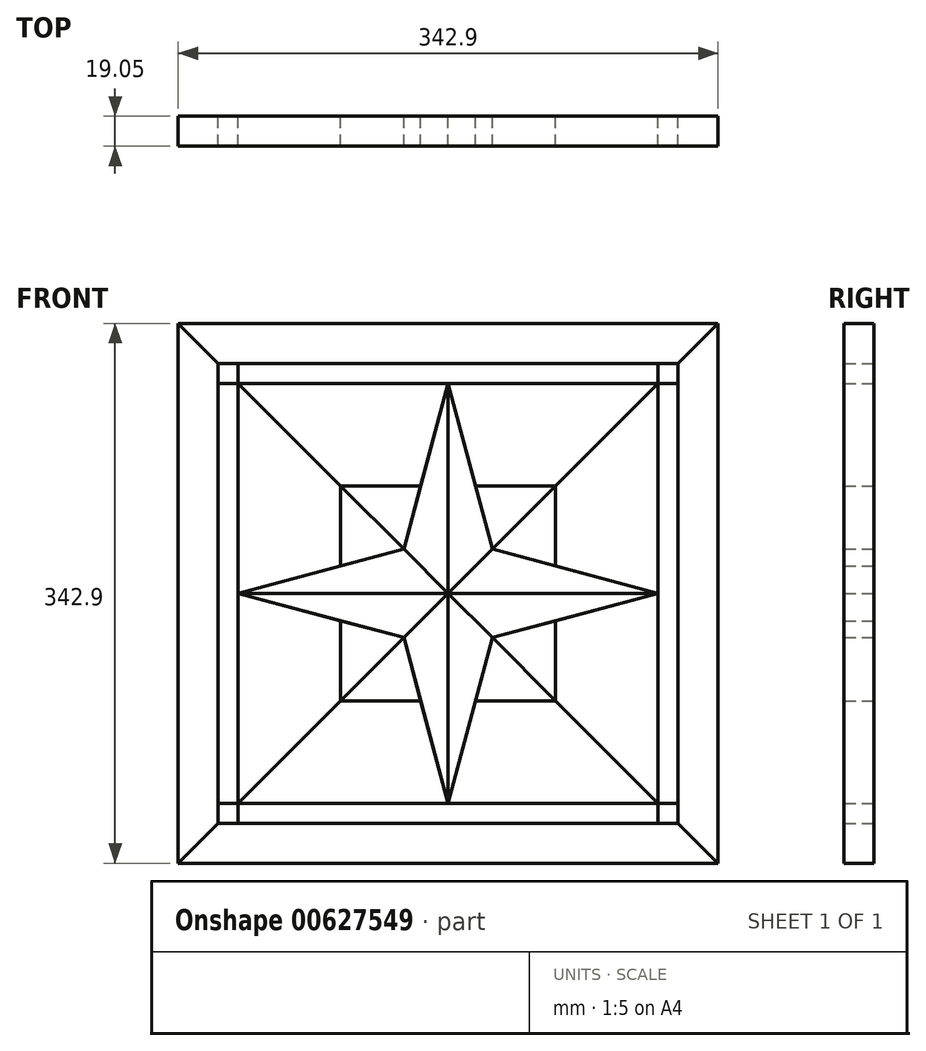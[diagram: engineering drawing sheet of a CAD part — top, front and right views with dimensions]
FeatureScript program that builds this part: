
annotation { "Feature Type Name" : "Feature", "Feature Type Description" : "" }
export const myFeature = defineFeature(function(context is Context, id is Id, definition is map)
    precondition{}
    {
        {
            var Q0;
            Q0=qCreatedBy(makeId("Front.planeOp"),FACE);
            var sketch = newSketch(context, id + "F0", { "sketchPlane" : qUnion([Q0])});
            skLineSegment(sketch, "E0", {"start": v(0, 133.35) * mm, "end": v(-28.18, 28.18) * mm});
            skLineSegment(sketch, "E1", {"start": v(-28.18, 28.18) * mm, "end": v(-133.35, 0) * mm});
            skLineSegment(sketch, "E2", {"start": v(-133.35, 0) * mm, "end": v(-28.18, -28.18) * mm});
            skLineSegment(sketch, "E3", {"start": v(-28.18, -28.18) * mm, "end": v(0, -133.35) * mm});
            skLineSegment(sketch, "E4", {"start": v(0, -133.35) * mm, "end": v(28.18, -28.18) * mm});
            skLineSegment(sketch, "E5", {"start": v(28.18, -28.18) * mm, "end": v(133.35, 0) * mm});
            skLineSegment(sketch, "E6", {"start": v(133.35, 0) * mm, "end": v(28.18, 28.18) * mm});
            skLineSegment(sketch, "E7", {"start": v(28.18, 28.18) * mm, "end": v(0, 133.35) * mm});
            skLineSegment(sketch, "E8", {"start": v(0, 133.35) * mm, "end": v(0, 0) * mm});
            skLineSegment(sketch, "E9", {"start": v(0, 0) * mm, "end": v(-28.18, 28.18) * mm});
            skLineSegment(sketch, "E10", {"start": v(0, 0) * mm, "end": v(28.18, 28.18) * mm});
            skLineSegment(sketch, "E11", {"start": v(0, 0) * mm, "end": v(-28.18, -28.18) * mm});
            skLineSegment(sketch, "E12", {"start": v(0, 0) * mm, "end": v(-133.35, 0) * mm});
            skLineSegment(sketch, "E13", {"start": v(0, 0) * mm, "end": v(28.18, -28.18) * mm});
            skLineSegment(sketch, "E14", {"start": v(0, 0) * mm, "end": v(133.35, 0) * mm});
            skLineSegment(sketch, "E15", {"start": v(17.44, 68.24) * mm, "end": v(68.24, 68.24) * mm});
            skLineSegment(sketch, "E16", {"start": v(68.24, 68.24) * mm, "end": v(68.24, 17.44) * mm});
            skLineSegment(sketch, "E17", {"start": v(28.18, 28.18) * mm, "end": v(68.24, 68.24) * mm});
            skLineSegment(sketch, "E18", {"start": v(-17.44, 68.24) * mm, "end": v(-68.24, 68.24) * mm});
            skLineSegment(sketch, "E19", {"start": v(-68.24, 68.24) * mm, "end": v(-68.24, 17.44) * mm});
            skLineSegment(sketch, "E20", {"start": v(-68.24, 68.24) * mm, "end": v(-28.18, 28.18) * mm});
            skLineSegment(sketch, "E21", {"start": v(0, 0) * mm, "end": v(0, -133.35) * mm});
            skLineSegment(sketch, "E22", {"start": v(-68.24, -17.44) * mm, "end": v(-68.24, -68.24) * mm});
            skLineSegment(sketch, "E23", {"start": v(-68.24, -68.24) * mm, "end": v(-17.44, -68.24) * mm});
            skLineSegment(sketch, "E24", {"start": v(-68.24, -68.24) * mm, "end": v(-28.18, -28.18) * mm});
            skLineSegment(sketch, "E25", {"start": v(17.44, -68.24) * mm, "end": v(68.24, -68.24) * mm});
            skLineSegment(sketch, "E26", {"start": v(68.24, -68.24) * mm, "end": v(68.24, -17.44) * mm});
            skLineSegment(sketch, "E27", {"start": v(68.24, -17.44) * mm, "end": v(28.18, -28.18) * mm});
            skLineSegment(sketch, "E28", {"start": v(68.24, -68.24) * mm, "end": v(28.18, -28.18) * mm});
            skLineSegment(sketch, "E29.bottom", {"start": v(171.45, -171.45) * mm, "end": v(-171.45, -171.45) * mm});
            skLineSegment(sketch, "E29.top", {"start": v(171.45, 171.45) * mm, "end": v(-171.45, 171.45) * mm});
            skLineSegment(sketch, "E29.left", {"start": v(171.45, -171.45) * mm, "end": v(171.45, 171.45) * mm});
            skLineSegment(sketch, "E29.right", {"start": v(-171.45, -171.45) * mm, "end": v(-171.45, 171.45) * mm});
            skPoint(sketch, "E29.middle", {"position": v(0, 0) * mm});
            skLineSegment(sketch, "E30", {"start": v(-171.45, 171.45) * mm, "end": v(-146.05, 146.05) * mm});
            skLineSegment(sketch, "E31", {"start": v(-146.05, 146.05) * mm, "end": v(-146.05, -146.05) * mm});
            skLineSegment(sketch, "E32", {"start": v(-146.05, -146.05) * mm, "end": v(-171.45, -171.45) * mm});
            skLineSegment(sketch, "E33", {"start": v(-146.05, 146.05) * mm, "end": v(146.05, 146.05) * mm});
            skLineSegment(sketch, "E34", {"start": v(146.05, 146.05) * mm, "end": v(171.45, 171.45) * mm});
            skLineSegment(sketch, "E35", {"start": v(146.05, 146.05) * mm, "end": v(146.05, -146.05) * mm});
            skLineSegment(sketch, "E36", {"start": v(146.05, -146.05) * mm, "end": v(-146.05, -146.05) * mm});
            skLineSegment(sketch, "E37", {"start": v(146.05, -146.05) * mm, "end": v(171.45, -171.45) * mm});
            skLineSegment(sketch, "E38", {"start": v(-133.35, 146.05) * mm, "end": v(-133.35, -146.05) * mm});
            skLineSegment(sketch, "E39", {"start": v(-146.05, 133.35) * mm, "end": v(146.05, 133.35) * mm});
            skLineSegment(sketch, "E40", {"start": v(133.35, 146.05) * mm, "end": v(133.35, -146.05) * mm});
            skLineSegment(sketch, "E41", {"start": v(-146.05, -133.35) * mm, "end": v(133.35, -133.35) * mm});
            skLineSegment(sketch, "E42", {"start": v(133.35, -133.35) * mm, "end": v(146.05, -133.35) * mm});
            skSolve(sketch);
        }
        {
            var Q0;
            Q0=makeQuery(id+"F0.imprint","IMPRINT",FACE,{"disambiguationData":[TD([[makeQuery(id+"F0.imprint","IMPRINT",EDGE,{"derivedFrom":sQuery(id+"F0.wireOp",EDGE,"E29.left")}),1.0]])]});
            var Q1;
            Q1=makeQuery(id+"F0.imprint","IMPRINT",FACE,{"disambiguationData":[TD([[makeQuery(id+"F0.imprint","IMPRINT",EDGE,{"derivedFrom":sQuery(id+"F0.wireOp",EDGE,"E29.right")}),-1.0]])]});
            extrude(context, id + "F1", {"entities" : qUnion([Q0, Q1]), "depth" : 19.05 * mm, "offsetDistance" : 25.4 * mm});
        }
        {
            var Q0;
            Q0=makeQuery(id+"F0.imprint","IMPRINT",FACE,{"disambiguationData":[TD([[makeQuery(id+"F0.imprint","IMPRINT",EDGE,{"derivedFrom":sQuery(id+"F0.wireOp",EDGE,"E29.top")}),1.0]])]});
            var Q1;
            Q1=makeQuery(id+"F0.imprint","IMPRINT",FACE,{"disambiguationData":[TD([[makeQuery(id+"F0.imprint","IMPRINT",EDGE,{"derivedFrom":sQuery(id+"F0.wireOp",EDGE,"E29.bottom")}),-1.0]])]});
            extrude(context, id + "F2", {"entities" : qUnion([Q0, Q1]), "depth" : 19.05 * mm, "offsetDistance" : 25.4 * mm});
        }
        {
            var Q0;
            {var subQ0=sQuery(id+"F0.wireOp",EDGE,"E8");Q0=makeQuery(id+"F0.imprint","IMPRINT",FACE,{"disambiguationData":[TD([[makeQuery(id+"F0.imprint","IMPRINT",EDGE,{"derivedFrom":subQ0}),-1.0]])]});}
            var Q1;
            {var subQ3=sQuery(id+"F0.wireOp",EDGE,"E10");Q1=makeQuery(id+"F0.imprint","IMPRINT",FACE,{"disambiguationData":[TD([[makeQuery(id+"F0.imprint","IMPRINT",EDGE,{"derivedFrom":subQ3}),-1.0]])]});}
            var Q2;
            {var subQ3=sQuery(id+"F0.wireOp",EDGE,"E13");Q2=makeQuery(id+"F0.imprint","IMPRINT",FACE,{"disambiguationData":[TD([[makeQuery(id+"F0.imprint","IMPRINT",EDGE,{"derivedFrom":subQ3}),-1.0]])]});}
            var Q3;
            {var subQ3=sQuery(id+"F0.wireOp",EDGE,"E11");Q3=makeQuery(id+"F0.imprint","IMPRINT",FACE,{"disambiguationData":[TD([[makeQuery(id+"F0.imprint","IMPRINT",EDGE,{"derivedFrom":subQ3}),-1.0]])]});}
            extrude(context, id + "F3", {"entities" : qUnion([Q0, Q1, Q2, Q3]), "depth" : 19.05 * mm, "offsetDistance" : 25.4 * mm});
        }
        {
            var Q0;
            {var subQ2=sQuery(id+"F0.wireOp",EDGE,"E15");Q0=makeQuery(id+"F0.imprint","IMPRINT",FACE,{"disambiguationData":[TD([[makeQuery(id+"F0.imprint","IMPRINT",EDGE,{"derivedFrom":subQ2}),-1.0]])]});}
            var Q1;
            Q1=makeQuery(id+"F0.imprint","IMPRINT",FACE,{"disambiguationData":[TD([[makeQuery(id+"F0.imprint","IMPRINT",EDGE,{"derivedFrom":sQuery(id+"F0.wireOp",EDGE,"E26")}),1.0]])]});
            var Q2;
            {var subQ2=sQuery(id+"F0.wireOp",EDGE,"E23");Q2=makeQuery(id+"F0.imprint","IMPRINT",FACE,{"disambiguationData":[TD([[makeQuery(id+"F0.imprint","IMPRINT",EDGE,{"derivedFrom":subQ2}),1.0]])]});}
            var Q3;
            {var subQ2=sQuery(id+"F0.wireOp",EDGE,"E19");Q3=makeQuery(id+"F0.imprint","IMPRINT",FACE,{"disambiguationData":[TD([[makeQuery(id+"F0.imprint","IMPRINT",EDGE,{"derivedFrom":subQ2}),1.0]])]});}
            extrude(context, id + "F4", {"entities" : qUnion([Q0, Q1, Q2, Q3]), "depth" : 19.05 * mm, "offsetDistance" : 25.4 * mm});
        }
        {
            var Q0;
            {var subQ2=sQuery(id+"F0.wireOp",EDGE,"E18");Q0=makeQuery(id+"F0.imprint","IMPRINT",FACE,{"disambiguationData":[TD([[makeQuery(id+"F0.imprint","IMPRINT",EDGE,{"derivedFrom":subQ2}),1.0]])]});}
            var Q1;
            {var subQ2=sQuery(id+"F0.wireOp",EDGE,"E16");Q1=makeQuery(id+"F0.imprint","IMPRINT",FACE,{"disambiguationData":[TD([[makeQuery(id+"F0.imprint","IMPRINT",EDGE,{"derivedFrom":subQ2}),-1.0]])]});}
            var Q2;
            {var subQ2=sQuery(id+"F0.wireOp",EDGE,"E25");Q2=makeQuery(id+"F0.imprint","IMPRINT",FACE,{"disambiguationData":[TD([[makeQuery(id+"F0.imprint","IMPRINT",EDGE,{"derivedFrom":subQ2}),1.0]])]});}
            var Q3;
            {var subQ2=sQuery(id+"F0.wireOp",EDGE,"E22");Q3=makeQuery(id+"F0.imprint","IMPRINT",FACE,{"disambiguationData":[TD([[makeQuery(id+"F0.imprint","IMPRINT",EDGE,{"derivedFrom":subQ2}),1.0]])]});}
            extrude(context, id + "F5", {"entities" : qUnion([Q0, Q1, Q2, Q3]), "depth" : 19.05 * mm, "offsetDistance" : 25.4 * mm});
        }
        {
            var Q0;
            {var subQ3=sQuery(id+"F0.wireOp",EDGE,"E8");Q0=makeQuery(id+"F0.imprint","IMPRINT",FACE,{"disambiguationData":[TD([[makeQuery(id+"F0.imprint","IMPRINT",EDGE,{"derivedFrom":subQ3}),1.0]])]});}
            var Q1;
            Q1=makeQuery(id+"F0.imprint","IMPRINT",FACE,{"disambiguationData":[TD([[makeQuery(id+"F0.imprint","IMPRINT",EDGE,{"derivedFrom":sQuery(id+"F0.wireOp",EDGE,"E5")}),1.0]])]});
            var Q2;
            {var subQ0=sQuery(id+"F0.wireOp",EDGE,"E11");Q2=makeQuery(id+"F0.imprint","IMPRINT",FACE,{"disambiguationData":[TD([[makeQuery(id+"F0.imprint","IMPRINT",EDGE,{"derivedFrom":subQ0}),1.0]])]});}
            var Q3;
            {var subQ0=sQuery(id+"F0.wireOp",EDGE,"E9");Q3=makeQuery(id+"F0.imprint","IMPRINT",FACE,{"disambiguationData":[TD([[makeQuery(id+"F0.imprint","IMPRINT",EDGE,{"derivedFrom":subQ0}),1.0]])]});}
            extrude(context, id + "F6", {"entities" : qUnion([Q0, Q1, Q2, Q3]), "depth" : 19.05 * mm, "offsetDistance" : 25.4 * mm});
        }
        {
            var Q0;
            {var subQ0=sQuery(id+"F0.wireOp",EDGE,"E33");var subQ5=sQuery(id+"F0.wireOp",EDGE,"E38");var subQ6=makeQuery(id+"F0.imprint","INTERSECT",VERTEX,{"derivedFrom":[subQ0,subQ5]});Q0=makeQuery(id+"F0.imprint","IMPRINT",FACE,{"disambiguationData":[TD([[makeQuery(id+"F0.imprint","IMPRINT",EDGE,{"disambiguationData":[TD([[subQ6,-1.0]])],"derivedFrom":subQ5}),-1.0]])]});}
            var Q1;
            {var subQ0=sQuery(id+"F0.wireOp",EDGE,"E35");var subQ5=sQuery(id+"F0.wireOp",EDGE,"E39");var subQ6=makeQuery(id+"F0.imprint","INTERSECT",VERTEX,{"derivedFrom":[subQ0,subQ5]});Q1=makeQuery(id+"F0.imprint","IMPRINT",FACE,{"disambiguationData":[TD([[makeQuery(id+"F0.imprint","IMPRINT",EDGE,{"disambiguationData":[TD([[subQ6,1.0]])],"derivedFrom":subQ5}),1.0]])]});}
            var Q2;
            {var subQ3=sQuery(id+"F0.wireOp",EDGE,"E42");Q2=makeQuery(id+"F0.imprint","IMPRINT",FACE,{"disambiguationData":[TD([[makeQuery(id+"F0.imprint","IMPRINT",EDGE,{"derivedFrom":subQ3}),-1.0]])]});}
            var Q3;
            {var subQ0=sQuery(id+"F0.wireOp",EDGE,"E36");var subQ5=sQuery(id+"F0.wireOp",EDGE,"E38");var subQ7=makeQuery(id+"F0.imprint","INTERSECT",VERTEX,{"derivedFrom":[subQ0,subQ5]});Q3=makeQuery(id+"F0.imprint","IMPRINT",FACE,{"disambiguationData":[TD([[makeQuery(id+"F0.imprint","IMPRINT",EDGE,{"disambiguationData":[TD([[subQ7,1.0]])],"derivedFrom":subQ5}),-1.0]])]});}
            extrude(context, id + "F7", {"entities" : qUnion([Q0, Q1, Q2, Q3]), "depth" : 19.05 * mm, "offsetDistance" : 25.4 * mm});
        }
        {
            var Q0;
            {var subQ4=sQuery(id+"F0.wireOp",EDGE,"E38");var subQ6=sQuery(id+"F0.wireOp",EDGE,"E33");var subQ7=makeQuery(id+"F0.imprint","INTERSECT",VERTEX,{"derivedFrom":[subQ6,subQ4]});Q0=makeQuery(id+"F0.imprint","IMPRINT",FACE,{"disambiguationData":[TD([[makeQuery(id+"F0.imprint","IMPRINT",EDGE,{"disambiguationData":[TD([[subQ7,-1.0]])],"derivedFrom":subQ6}),-1.0]])]});}
            var Q1;
            {var subQ2=sQuery(id+"F0.wireOp",EDGE,"E42");Q1=makeQuery(id+"F0.imprint","IMPRINT",FACE,{"disambiguationData":[TD([[makeQuery(id+"F0.imprint","IMPRINT",EDGE,{"derivedFrom":subQ2}),1.0]])]});}
            var Q2;
            {var subQ1=sQuery(id+"F0.wireOp",EDGE,"E36");var subQ6=sQuery(id+"F0.wireOp",EDGE,"E38");var subQ8=makeQuery(id+"F0.imprint","INTERSECT",VERTEX,{"derivedFrom":[subQ1,subQ6]});Q2=makeQuery(id+"F0.imprint","IMPRINT",FACE,{"disambiguationData":[TD([[makeQuery(id+"F0.imprint","IMPRINT",EDGE,{"disambiguationData":[TD([[subQ8,1.0]])],"derivedFrom":subQ1}),-1.0]])]});}
            var Q3;
            {var subQ0=sQuery(id+"F0.wireOp",EDGE,"E39");var subQ1=sQuery(id+"F0.wireOp",EDGE,"E31");var subQ2=makeQuery(id+"F0.imprint","INTERSECT",VERTEX,{"derivedFrom":[subQ1,subQ0]});Q3=makeQuery(id+"F0.imprint","IMPRINT",FACE,{"disambiguationData":[TD([[makeQuery(id+"F0.imprint","IMPRINT",EDGE,{"disambiguationData":[TD([[subQ2,-1.0]])],"derivedFrom":subQ1}),1.0]])]});}
            extrude(context, id + "F8", {"entities" : qUnion([Q0, Q1, Q2, Q3]), "depth" : 19.05 * mm, "offsetDistance" : 25.4 * mm});
        }
        {
            var Q0;
            Q0=qCreatedBy(makeId("Front.planeOp"),FACE);
            var sketch = newSketch(context, id + "F9", { "sketchPlane" : qUnion([Q0])});
            skLineSegment(sketch, "E43", {"start": v(-133.35, 133.35) * mm, "end": v(-68.24, 68.24) * mm});
            skLineSegment(sketch, "E44", {"start": v(68.24, 68.24) * mm, "end": v(133.35, 133.35) * mm});
            skLineSegment(sketch, "E45", {"start": v(-68.24, -68.24) * mm, "end": v(-133.35, -133.35) * mm});
            skLineSegment(sketch, "E46", {"start": v(68.24, -68.24) * mm, "end": v(133.35, -133.35) * mm});
            skLineSegment(sketch, "E47.0", {"start": v(-133.35, 133.35) * mm, "end": v(133.35, 133.35) * mm});
            skLineSegment(sketch, "E48.0", {"start": v(17.44, 68.24) * mm, "end": v(68.24, 68.24) * mm});
            skLineSegment(sketch, "E49.0", {"start": v(17.44, 68.24) * mm, "end": v(0, 133.35) * mm});
            skPoint(sketch, "E50.orphan", {"position": v(28.18, 28.18) * mm});
            skLineSegment(sketch, "E51.0", {"start": v(0, 133.35) * mm, "end": v(-17.44, 68.24) * mm});
            skLineSegment(sketch, "E52.0", {"start": v(-17.44, 68.24) * mm, "end": v(-68.24, 68.24) * mm});
            skLineSegment(sketch, "E53.0", {"start": v(-68.24, 17.44) * mm, "end": v(-133.35, 0) * mm});
            skLineSegment(sketch, "E54.0", {"start": v(-133.35, 133.35) * mm, "end": v(-133.35, -133.35) * mm});
            skLineSegment(sketch, "E55.0", {"start": v(-68.24, -17.44) * mm, "end": v(-68.24, -68.24) * mm});
            skPoint(sketch, "E56.orphan", {"position": v(-28.18, 28.18) * mm});
            skLineSegment(sketch, "E57.0", {"start": v(-68.24, 68.24) * mm, "end": v(-68.24, 17.44) * mm});
            skLineSegment(sketch, "E58.0.0", {"start": v(-28.18, -28.18) * mm, "end": v(-68.24, -17.44) * mm});
            skLineSegment(sketch, "E59.0", {"start": v(-133.35, 0) * mm, "end": v(-68.24, -17.44) * mm});
            skPoint(sketch, "E60.orphan", {"position": v(-28.18, -28.18) * mm});
            skLineSegment(sketch, "E61.0", {"start": v(-133.35, -133.35) * mm, "end": v(133.35, -133.35) * mm});
            skLineSegment(sketch, "E62.0", {"start": v(-17.44, -68.24) * mm, "end": v(0, -133.35) * mm});
            skLineSegment(sketch, "E63.0", {"start": v(-68.24, -68.24) * mm, "end": v(-17.44, -68.24) * mm});
            skLineSegment(sketch, "E64.0.1", {"start": v(0, 0) * mm, "end": v(-28.18, -28.18) * mm});
            skLineSegment(sketch, "E65.0", {"start": v(17.44, -68.24) * mm, "end": v(68.24, -68.24) * mm});
            skLineSegment(sketch, "E66.0", {"start": v(68.24, -68.24) * mm, "end": v(68.24, -17.44) * mm});
            skLineSegment(sketch, "E67.0", {"start": v(133.35, 0) * mm, "end": v(68.24, -17.44) * mm});
            skLineSegment(sketch, "E68.0", {"start": v(0, -133.35) * mm, "end": v(17.44, -68.24) * mm});
            skLineSegment(sketch, "E69.0", {"start": v(133.35, 133.35) * mm, "end": v(133.35, -133.35) * mm});
            skPoint(sketch, "E70.orphan", {"position": v(28.18, -28.18) * mm});
            skLineSegment(sketch, "E71.0", {"start": v(68.24, 68.24) * mm, "end": v(68.24, 17.44) * mm});
            skLineSegment(sketch, "E72.0", {"start": v(133.35, 0) * mm, "end": v(68.24, 17.44) * mm});
            skSolve(sketch);
        }
        {
            var Q0;
            {var subQ0=sQuery(id+"F9.wireOp",EDGE,"E43");Q0=makeQuery(id+"F9.imprint","IMPRINT",FACE,{"disambiguationData":[TD([[makeQuery(id+"F9.imprint","IMPRINT",EDGE,{"derivedFrom":subQ0}),1.0]])]});}
            var Q1;
            {var subQ0=sQuery(id+"F9.wireOp",EDGE,"E44");Q1=makeQuery(id+"F9.imprint","IMPRINT",FACE,{"disambiguationData":[TD([[makeQuery(id+"F9.imprint","IMPRINT",EDGE,{"derivedFrom":subQ0}),1.0]])]});}
            extrude(context, id + "F10", {"entities" : qUnion([Q0, Q1]), "depth" : 19.05 * mm, "offsetDistance" : 25.4 * mm});
        }
        {
            var Q0;
            {var subQ0=sQuery(id+"F9.wireOp",EDGE,"E43");Q0=makeQuery(id+"F9.imprint","IMPRINT",FACE,{"disambiguationData":[TD([[makeQuery(id+"F9.imprint","IMPRINT",EDGE,{"derivedFrom":subQ0}),-1.0]])]});}
            var Q1;
            {var subQ0=sQuery(id+"F9.wireOp",EDGE,"E45");Q1=makeQuery(id+"F9.imprint","IMPRINT",FACE,{"disambiguationData":[TD([[makeQuery(id+"F9.imprint","IMPRINT",EDGE,{"derivedFrom":subQ0}),-1.0]])]});}
            extrude(context, id + "F11", {"entities" : qUnion([Q0, Q1]), "depth" : 19.05 * mm, "offsetDistance" : 25.4 * mm});
        }
        {
            var Q0;
            {var subQ0=sQuery(id+"F9.wireOp",EDGE,"E44");Q0=makeQuery(id+"F9.imprint","IMPRINT",FACE,{"disambiguationData":[TD([[makeQuery(id+"F9.imprint","IMPRINT",EDGE,{"derivedFrom":subQ0}),-1.0]])]});}
            var Q1;
            {var subQ0=sQuery(id+"F9.wireOp",EDGE,"E46");Q1=makeQuery(id+"F9.imprint","IMPRINT",FACE,{"disambiguationData":[TD([[makeQuery(id+"F9.imprint","IMPRINT",EDGE,{"derivedFrom":subQ0}),1.0]])]});}
            extrude(context, id + "F12", {"entities" : qUnion([Q0, Q1]), "depth" : 19.05 * mm, "offsetDistance" : 25.4 * mm});
        }
        {
            var Q0;
            {var subQ0=sQuery(id+"F9.wireOp",EDGE,"E45");Q0=makeQuery(id+"F9.imprint","IMPRINT",FACE,{"disambiguationData":[TD([[makeQuery(id+"F9.imprint","IMPRINT",EDGE,{"derivedFrom":subQ0}),1.0]])]});}
            var Q1;
            {var subQ0=sQuery(id+"F9.wireOp",EDGE,"E46");Q1=makeQuery(id+"F9.imprint","IMPRINT",FACE,{"disambiguationData":[TD([[makeQuery(id+"F9.imprint","IMPRINT",EDGE,{"derivedFrom":subQ0}),-1.0]])]});}
            extrude(context, id + "F13", {"entities" : qUnion([Q0, Q1]), "depth" : 19.05 * mm, "offsetDistance" : 25.4 * mm});
        }
    });
